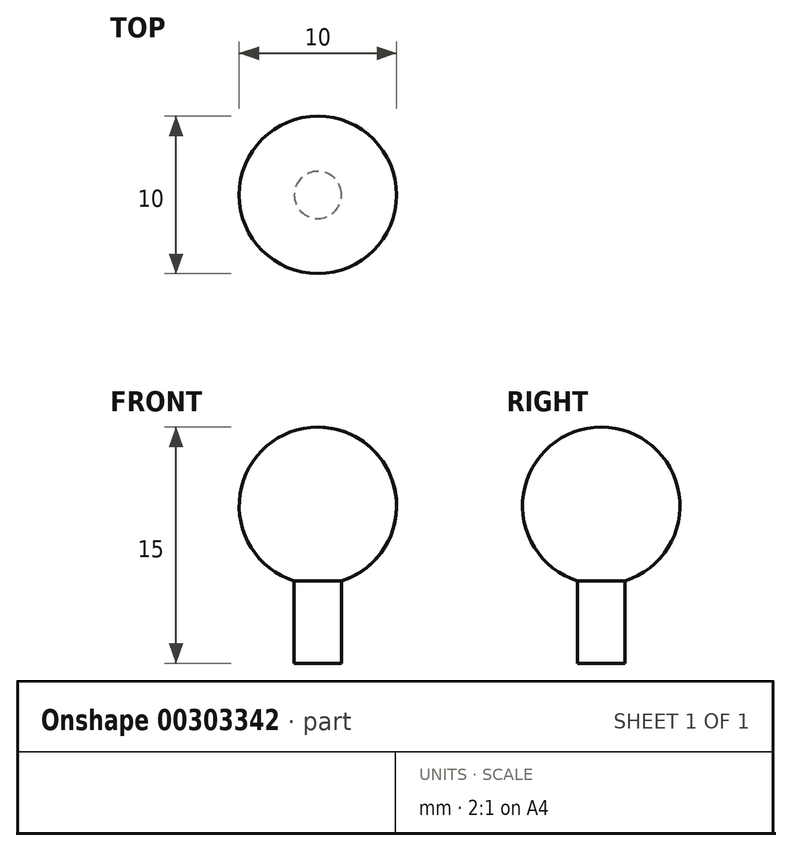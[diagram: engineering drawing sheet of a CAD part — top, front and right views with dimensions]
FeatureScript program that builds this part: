
annotation { "Feature Type Name" : "Feature", "Feature Type Description" : "" }
export const myFeature = defineFeature(function(context is Context, id is Id, definition is map)
    precondition{}
    {
        {
            var Q0;
            Q0=qCreatedBy(makeId("Front.planeOp"),FACE);
            var sketch = newSketch(context, id + "F0", { "sketchPlane" : qUnion([Q0])});
            skArc(sketch, "E0", {"start": v(1.5, -4.77) * mm, "mid": v(4.94, 0.76) * mm, "end": v(0, 5) * mm});
            skLineSegment(sketch, "E1.top", {"start": v(0, -10) * mm, "end": v(1.5, -10) * mm});
            skLineSegment(sketch, "E1.right", {"start": v(1.5, -4.77) * mm, "end": v(1.5, -10) * mm});
            skPoint(sketch, "E1.bottom.end.orphan", {"position": v(1.5, 10) * mm});
            skPoint(sketch, "E1.bottom.start.orphan", {"position": v(-1.5, 10) * mm});
            skLineSegment(sketch, "E2", {"start": v(0, 5) * mm, "end": v(0, -10) * mm});
            skPoint(sketch, "E3.orphan", {"position": v(-1.5, -10) * mm});
            skSolve(sketch);
        }
        {
            var Q0;
            Q0 = qSketchRegion(id + "F0", true);
            var Q1;
            Q1=sQuery(id+"F0.wireOp",EDGE,"E2");
            revolve(context, id + "F1", {"entities" : qUnion([Q0]), "axis" : qUnion([Q1]), "revolveType" : RevolveType.FULL});
        }
    });
